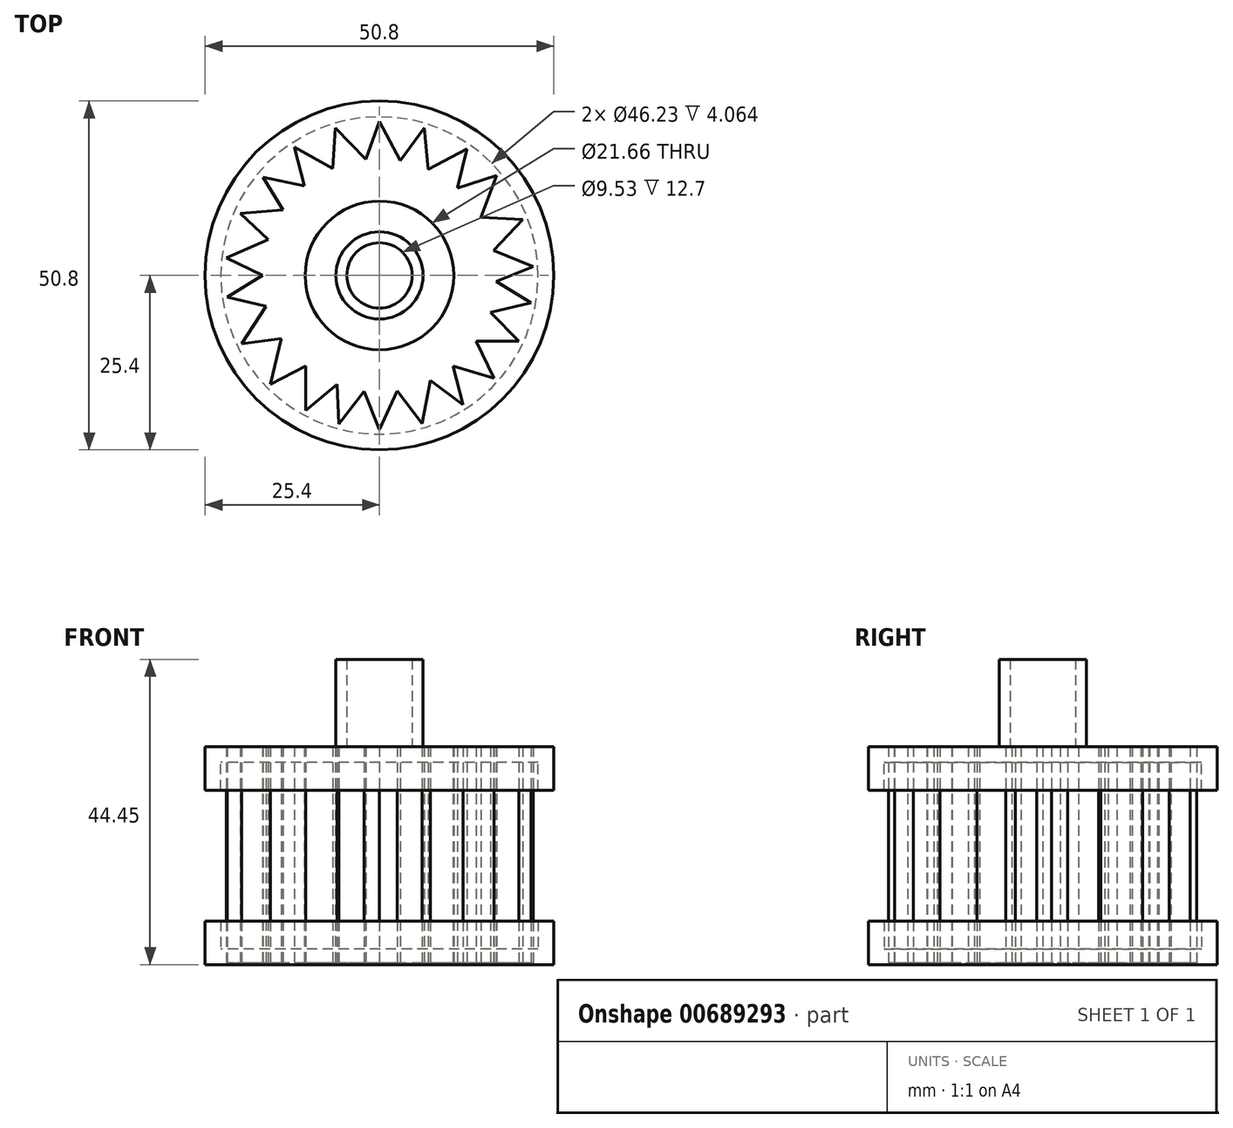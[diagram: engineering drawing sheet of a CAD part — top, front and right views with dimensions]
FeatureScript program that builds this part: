
annotation { "Feature Type Name" : "Feature", "Feature Type Description" : "" }
export const myFeature = defineFeature(function(context is Context, id is Id, definition is map)
    precondition{}
    {
        {
            var Q0;
            Q0=qCreatedBy(makeId("Top.planeOp"),FACE);
            var sketch = newSketch(context, id + "F0", { "sketchPlane" : qUnion([Q0])});
            skCircle(sketch, "E0", {"center": v(0, 0) * mm, "radius": 6.35 * mm});
            skCircle(sketch, "E1", {"center": v(0, 0) * mm, "radius": 4.76 * mm});
            skSolve(sketch);
        }
        {
            var Q0;
            Q0=makeQuery(id+"F0.imprint","IMPRINT",FACE,{"disambiguationData":[TD([[makeQuery(id+"F0.imprint","IMPRINT",EDGE,{"derivedFrom":sQuery(id+"F0.wireOp",EDGE,"E0")}),1.0]])]});
            extrude(context, id + "F1", {"entities" : qUnion([Q0]), "depth" : 12.7 * mm, "offsetDistance" : 25.4 * mm});
        }
        {
            var Q0;
            Q0=qCreatedBy(makeId("Top.planeOp"),FACE);
            var sketch = newSketch(context, id + "F2", { "sketchPlane" : qUnion([Q0])});
            skCircle(sketch, "E2", {"center": v(0, 0) * mm, "radius": 25.4 * mm});
            skSolve(sketch);
        }
        {
            var Q0;
            Q0=makeQuery(id+"F2.imprint","IMPRINT",FACE,{"disambiguationData":[TD([[makeQuery(id+"F2.imprint","IMPRINT",EDGE,{"derivedFrom":sQuery(id+"F2.wireOp",EDGE,"E2")}),1.0]])]});
            extrude(context, id + "F3", {"entities" : qUnion([Q0]), "operationType" : NewBodyOperationType.ADD, "oppositeDirection" : true, "depth" : 6.35 * mm, "offsetDistance" : 25.4 * mm});
        }
        {
            var Q0;
            Q0=makeQuery(id+"F3.opExtrude","CAP_FACE",FACE,{"disambiguationData":[OSD([sQuery(id+"F2.wireOp",EDGE,"E2")])],"isStart":false});
            shell(context, id + "F4", {"entities" : qUnion([Q0]), "thickness" : 2.3 * mm});
        }
        {
            var Q0;
            Q0=qCreatedBy(makeId("Top.planeOp"),FACE);
            cPlane(context, id + "F5", {"entities" : qUnion([Q0]), "cplaneType" : CPlaneType.OFFSET, "offset" : 31.75 * mm, "oppositeDirection" : true, "width" : 152.4 * mm, "height" : 152.4 * mm});
        }
        {
            var Q0;
            Q0=qCreatedBy(id+"F5.planeOp",FACE);
            var sketch = newSketch(context, id + "F6", { "sketchPlane" : qUnion([Q0])});
            skCircle(sketch, "E3", {"center": v(0, 0) * mm, "radius": 25.4 * mm});
            skSolve(sketch);
        }
        {
            var Q0;
            Q0 = qSketchRegion(id + "F6", true);
            extrude(context, id + "F7", {"entities" : qUnion([Q0]), "depth" : 6.35 * mm, "offsetDistance" : 25.4 * mm});
        }
        {
            var Q0;
            Q0=makeQuery(id+"F7.opExtrude","CAP_FACE",FACE,{"disambiguationData":[OSD([sQuery(id+"F6.wireOp",EDGE,"E3")])],"isStart":false});
            shell(context, id + "F8", {"entities" : qUnion([Q0]), "thickness" : 2.3 * mm});
        }
        {
            var Q0;
            Q0=qCreatedBy(makeId("Top.planeOp"),FACE);
            var sketch = newSketch(context, id + "F9", { "sketchPlane" : qUnion([Q0])});
            skLineSegment(sketch, "E4", {"start": v(-17.02, 0) * mm, "end": v(-22.28, 2.58) * mm});
            skLineSegment(sketch, "E5", {"start": v(-22.28, 2.58) * mm, "end": v(-16.2, 5.23) * mm});
            skLineSegment(sketch, "E6", {"start": v(-16.2, 5.23) * mm, "end": v(-20.3, 9.03) * mm});
            skLineSegment(sketch, "E7", {"start": v(-20.3, 9.03) * mm, "end": v(-14.07, 9.57) * mm});
            skLineSegment(sketch, "E8", {"start": v(-14.07, 9.57) * mm, "end": v(-16.97, 14.3) * mm});
            skLineSegment(sketch, "E9", {"start": v(-16.97, 14.3) * mm, "end": v(-10.94, 13.04) * mm});
            skLineSegment(sketch, "E10", {"start": v(-10.94, 13.04) * mm, "end": v(-12.4, 18.69) * mm});
            skLineSegment(sketch, "E11", {"start": v(-12.4, 18.69) * mm, "end": v(-6.81, 15.6) * mm});
            skLineSegment(sketch, "E12", {"start": v(-6.81, 15.6) * mm, "end": v(-6.42, 21.5) * mm});
            skLineSegment(sketch, "E13", {"start": v(-6.42, 21.5) * mm, "end": v(-1.97, 16.9) * mm});
            skLineSegment(sketch, "E14", {"start": v(-1.97, 16.9) * mm, "end": v(0, 22.43) * mm});
            skLineSegment(sketch, "E15", {"start": v(0, 22.43) * mm, "end": v(3.03, 16.75) * mm});
            skLineSegment(sketch, "E16", {"start": v(3.03, 16.75) * mm, "end": v(6.5, 21.47) * mm});
            skLineSegment(sketch, "E17", {"start": v(6.5, 21.47) * mm, "end": v(7.09, 15.47) * mm});
            skLineSegment(sketch, "E18", {"start": v(7.09, 15.47) * mm, "end": v(12.76, 18.44) * mm});
            skLineSegment(sketch, "E19", {"start": v(12.76, 18.44) * mm, "end": v(11.34, 12.7) * mm});
            skLineSegment(sketch, "E20", {"start": v(11.34, 12.7) * mm, "end": v(17.04, 14.59) * mm});
            skLineSegment(sketch, "E21", {"start": v(17.04, 14.59) * mm, "end": v(14.75, 8.5) * mm});
            skLineSegment(sketch, "E22", {"start": v(14.75, 8.5) * mm, "end": v(20.88, 8.18) * mm});
            skLineSegment(sketch, "E23", {"start": v(20.88, 8.18) * mm, "end": v(16.62, 3.65) * mm});
            skLineSegment(sketch, "E24", {"start": v(16.62, 3.65) * mm, "end": v(22.4, 1.27) * mm});
            skLineSegment(sketch, "E25", {"start": v(22.4, 1.27) * mm, "end": v(17, -0.86) * mm});
            skLineSegment(sketch, "E26", {"start": v(17, -0.86) * mm, "end": v(22.08, -3.95) * mm});
            skLineSegment(sketch, "E27", {"start": v(22.08, -3.95) * mm, "end": v(16.15, -5.38) * mm});
            skLineSegment(sketch, "E28", {"start": v(16.15, -5.38) * mm, "end": v(20.28, -9.58) * mm});
            skLineSegment(sketch, "E29", {"start": v(20.28, -9.58) * mm, "end": v(14.07, -9.58) * mm});
            skLineSegment(sketch, "E30", {"start": v(14.07, -9.58) * mm, "end": v(16.7, -14.97) * mm});
            skLineSegment(sketch, "E31", {"start": v(16.7, -14.97) * mm, "end": v(10.73, -13.21) * mm});
            skLineSegment(sketch, "E32", {"start": v(10.73, -13.21) * mm, "end": v(12.18, -18.83) * mm});
            skLineSegment(sketch, "E33", {"start": v(12.18, -18.83) * mm, "end": v(7.43, -15.31) * mm});
            skLineSegment(sketch, "E34", {"start": v(7.43, -15.31) * mm, "end": v(6.19, -21.56) * mm});
            skLineSegment(sketch, "E35", {"start": v(6.19, -21.56) * mm, "end": v(2.6, -16.82) * mm});
            skLineSegment(sketch, "E36", {"start": v(2.6, -16.82) * mm, "end": v(0, -22.43) * mm});
            skLineSegment(sketch, "E37", {"start": v(0, -22.43) * mm, "end": v(-2.27, -16.87) * mm});
            skLineSegment(sketch, "E38", {"start": v(-2.27, -16.87) * mm, "end": v(-5.92, -21.63) * mm});
            skLineSegment(sketch, "E39", {"start": v(-5.92, -21.63) * mm, "end": v(-6.18, -15.86) * mm});
            skLineSegment(sketch, "E40", {"start": v(-6.18, -15.86) * mm, "end": v(-10.78, -19.67) * mm});
            skLineSegment(sketch, "E41", {"start": v(-10.78, -19.67) * mm, "end": v(-10.78, -13.17) * mm});
            skLineSegment(sketch, "E42", {"start": v(-10.78, -13.17) * mm, "end": v(-15.86, -15.86) * mm});
            skLineSegment(sketch, "E43", {"start": v(-15.86, -15.86) * mm, "end": v(-14.33, -9.19) * mm});
            skLineSegment(sketch, "E44", {"start": v(-14.33, -9.19) * mm, "end": v(-20.1, -9.97) * mm});
            skLineSegment(sketch, "E45", {"start": v(-20.1, -9.97) * mm, "end": v(-16.52, -4.49) * mm});
            skLineSegment(sketch, "E46", {"start": v(-16.52, -4.49) * mm, "end": v(-22.2, -3.16) * mm});
            skLineSegment(sketch, "E47", {"start": v(-22.2, -3.16) * mm, "end": v(-17.02, 0) * mm});
            skCircle(sketch, "E48", {"center": v(0, 0) * mm, "radius": 10.83 * mm});
            skSolve(sketch);
        }
        {
            var Q0;
            Q0=qCreatedBy(makeId("Right.planeOp"),FACE);
            var sketch = newSketch(context, id + "F10", { "sketchPlane" : qUnion([Q0])});
            skLineSegment(sketch, "E49", {"start": v(0, 0) * mm, "end": v(0, -31.51) * mm});
            skSolve(sketch);
        }
        {
            var Q0;
            Q0=makeQuery(id+"F9.imprint","IMPRINT",FACE,{"disambiguationData":[TD([[makeQuery(id+"F9.imprint","IMPRINT",EDGE,{"derivedFrom":sQuery(id+"F9.wireOp",EDGE,"E4")}),-1.0]])]});
            var Q1;
            Q1=sQuery(id+"F10.wireOp",EDGE,"E49");
            sweep(context, id + "F11", {"profiles" : qUnion([Q0]), "path" : qUnion([Q1])});
        }
    });
